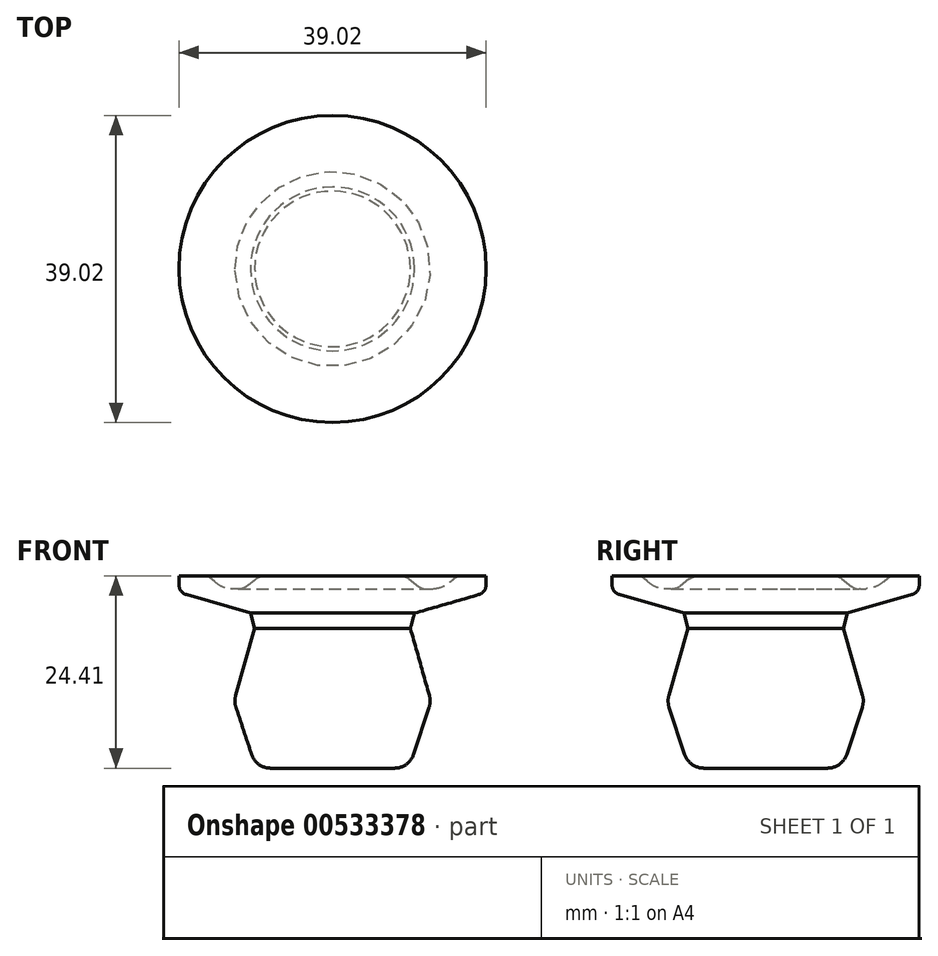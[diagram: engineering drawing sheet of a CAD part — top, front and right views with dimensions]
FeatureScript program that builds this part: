
annotation { "Feature Type Name" : "Feature", "Feature Type Description" : "" }
export const myFeature = defineFeature(function(context is Context, id is Id, definition is map)
    precondition{}
    {
        {
            var Q0;
            Q0=qCreatedBy(makeId("Front.planeOp"),FACE);
            var sketch = newSketch(context, id + "F0", { "sketchPlane" : qUnion([Q0])});
            skLineSegment(sketch, "E0", {"start": v(0, 0) * mm, "end": v(-9.71, 0) * mm});
            skLineSegment(sketch, "E1", {"start": v(-9.71, 0) * mm, "end": v(-12.51, 8.49) * mm});
            skLineSegment(sketch, "E2", {"start": v(-12.51, 8.49) * mm, "end": v(-9.89, 17.76) * mm});
            skLineSegment(sketch, "E3", {"start": v(-9.89, 17.76) * mm, "end": v(-10.41, 19.69) * mm});
            skLineSegment(sketch, "E4", {"start": v(-10.41, 19.69) * mm, "end": v(-19.51, 22.31) * mm});
            skLineSegment(sketch, "E5", {"start": v(-19.51, 22.31) * mm, "end": v(-19.51, 24.41) * mm});
            skLineSegment(sketch, "E6", {"start": v(-19.51, 24.41) * mm, "end": v(-15.84, 24.41) * mm});
            skLineSegment(sketch, "E7", {"start": v(-15.84, 24.41) * mm, "end": v(-14.04, 22.87) * mm});
            skLineSegment(sketch, "E8", {"start": v(-14.04, 22.87) * mm, "end": v(-11.4, 22.72) * mm});
            skLineSegment(sketch, "E9", {"start": v(-11.4, 22.72) * mm, "end": v(-9.19, 24.41) * mm});
            skLineSegment(sketch, "E10", {"start": v(-9.19, 24.41) * mm, "end": v(0, 24.41) * mm});
            skLineSegment(sketch, "E11", {"start": v(0, 24.41) * mm, "end": v(0, 0) * mm});
            skSolve(sketch);
        }
        {
            var Q0;
            Q0=makeQuery(id+"F0.imprint","IMPRINT",FACE,{"disambiguationData":[TD([[makeQuery(id+"F0.imprint","IMPRINT",EDGE,{"derivedFrom":sQuery(id+"F0.wireOp",EDGE,"E0")}),-1.0]])]});
            var Q1;
            Q1=sQuery(id+"F0.wireOp",EDGE,"E11");
            revolve(context, id + "F1", {"entities" : qUnion([Q0]), "axis" : qUnion([Q1]), "revolveType" : RevolveType.FULL});
        }
        {
            var Q0;
            Q0=makeQuery(id+"F1.opRevolve","SWEPT_EDGE",EDGE,{"disambiguationData":[OSD([sQuery(id+"F0.wireOp",EDGE,"E9"),sQuery(id+"F0.wireOp",EDGE,"E10")])]});
            fillet(context, id + "F2", {"entities" : qUnion([Q0]), "radius" : 1.98 * mm, "tangentPropagation" : true, "allowEdgeOverflow" : false});
        }
        {
            var Q0;
            Q0=makeQuery(id+"F1.opRevolve","SWEPT_EDGE",EDGE,{"disambiguationData":[OSD([sQuery(id+"F0.wireOp",EDGE,"E7"),sQuery(id+"F0.wireOp",EDGE,"E8")])]});
            fillet(context, id + "F3", {"entities" : qUnion([Q0]), "radius" : 3.8 * mm, "tangentPropagation" : true, "allowEdgeOverflow" : false});
        }
        {
            var Q0;
            Q0=makeQuery(id+"F1.opRevolve","SWEPT_EDGE",EDGE,{"disambiguationData":[OSD([sQuery(id+"F0.wireOp",EDGE,"E8"),sQuery(id+"F0.wireOp",EDGE,"E9")])]});
            fillet(context, id + "F4", {"entities" : qUnion([Q0]), "radius" : 1.65 * mm, "tangentPropagation" : true, "allowEdgeOverflow" : false});
        }
        {
            var Q0;
            Q0=makeQuery(id+"F1.opRevolve","SWEPT_EDGE",EDGE,{"disambiguationData":[OSD([sQuery(id+"F0.wireOp",EDGE,"E6"),sQuery(id+"F0.wireOp",EDGE,"E7")])]});
            fillet(context, id + "F5", {"entities" : qUnion([Q0]), "radius" : 1.05 * mm, "tangentPropagation" : true, "allowEdgeOverflow" : false});
        }
        {
            var Q0;
            Q0=makeQuery(id+"F1.opRevolve","SWEPT_EDGE",EDGE,{"disambiguationData":[OSD([sQuery(id+"F0.wireOp",EDGE,"E4"),sQuery(id+"F0.wireOp",EDGE,"E5")])]});
            fillet(context, id + "F6", {"entities" : qUnion([Q0]), "radius" : 1.31 * mm, "tangentPropagation" : true, "allowEdgeOverflow" : false});
        }
        {
            var Q0;
            Q0=makeQuery(id+"F1.opRevolve","SWEPT_FACE",FACE,{"disambiguationData":[OSD([sQuery(id+"F0.wireOp",EDGE,"E1")])]});
            fillet(context, id + "F7", {"entities" : qUnion([Q0]), "radius" : 2.56 * mm, "tangentPropagation" : true, "allowEdgeOverflow" : false});
        }
    });
